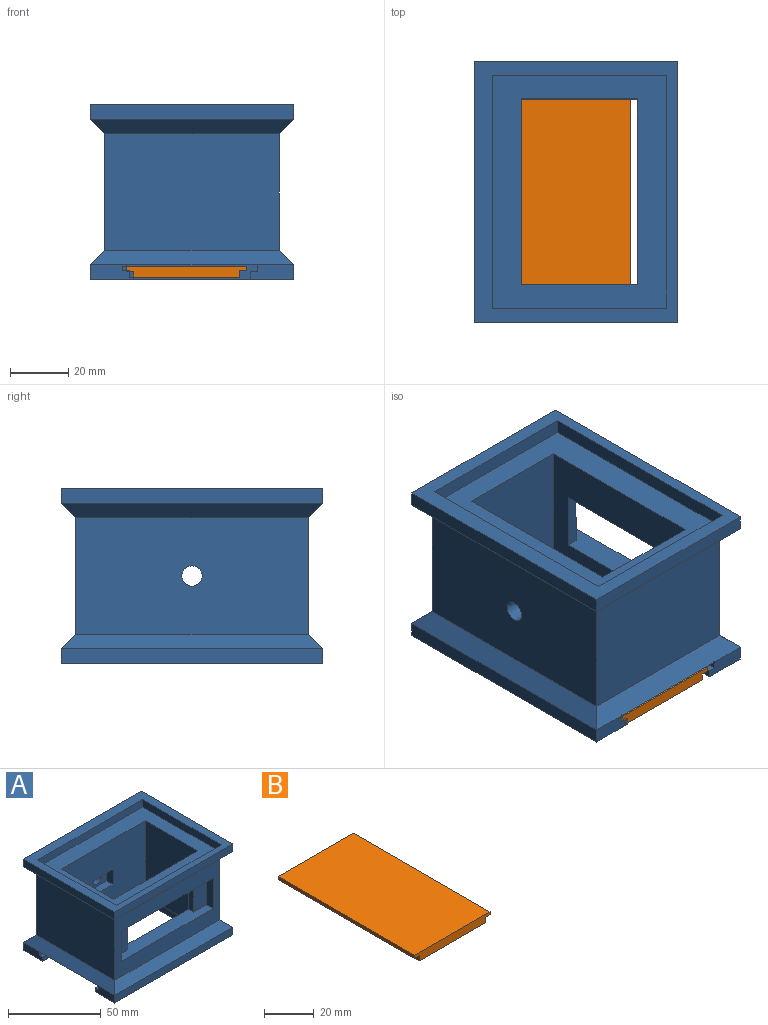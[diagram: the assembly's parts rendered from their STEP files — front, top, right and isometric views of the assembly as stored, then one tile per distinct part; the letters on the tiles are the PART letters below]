
ASSEMBLY  parts=2 mates=1
PART A: 58 faces, bbox 90x70x60 mm
  f0: plane 64x50mm, normal (0,-1,0), area 3050mm2, adj f7,f39,f40,f48,f52,f53,f54,f55
  f1: plane 64x2.5mm, normal (0,1,0), area 160mm2, adj f3,f4,f8,f46
  f2: plane 15x5mm, normal (-1,0,0), area 68.8mm2, adj f8,f13,f21,f43,f46,f47
  f3: plane 2.5x1.11mm, normal (-1,0,0), area 2.8mm2, adj f1,f8,f45,f46
  f4: plane 2.5x1.11mm, normal (1,0,0), area 2.8mm2, adj f1,f8,f43,f46
  f5: plane 20x10mm, normal (0,-1,0), area 200mm2, adj f30,f31,f32,f41
  f6: plane 64x50mm, normal (0,1,0), area 2200mm2, adj f7,f30,f32,f39,f40,f41,f42,f48
  f7: plane 80x60mm, normal (0,0,1), area 2240mm2, adj f0,f6,f35,f36,f37,f38,f39,f40
  f8: plane 90x70mm, normal (0,0,-1), area 3108.9mm2, adj f1,f2,f3,f4,f11,f12,f13,f14
  f9: plane 90x70mm, normal (0,0,1), area 1500mm2, adj f22,f23,f24,f25,f35,f36,f37,f38
  f10: plane 80x40mm, normal (0,-1,0), area 1800mm2, adj f15,f17,f20,f27,f30,f31,f32,f33
  f11: plane 90x5mm, normal (0,1,0), area 450mm2, adj f8,f12,f14,f19
  f12: plane 15x5mm, normal (-1,0,0), area 68.7mm2, adj f8,f11,f21,f44,f49,f50
  f13: plane 90x5mm, normal (0,-1,0), area 450mm2, adj f2,f8,f14,f20
  f14: plane 70x5mm, normal (1,0,0), area 350mm2, adj f8,f11,f13,f18
  f15: plane 60x40mm, normal (1,0,0), area 2400mm2, adj f10,f16,f18,f26
  f16: plane 80x40mm, normal (0,1,0), area 3161.5mm2, adj f15,f17,f19,f28,f57
  f17: plane 60x40mm, normal (-1,0,0), area 2400mm2, adj f10,f16,f21,f29
  f18: plane 70x5mm, normal (0.71,0,0.71), area 459.6mm2, adj f14,f15,f19,f20
  f19: plane 90x5mm, normal (0,0.71,0.71), area 601mm2, adj f11,f16,f18,f21
  f20: plane 90x5mm, normal (0,-0.71,0.71), area 601mm2, adj f10,f13,f18,f21
  f21: plane 70x5mm, normal (-0.71,0,0.71), area 459.6mm2, adj f2,f12,f17,f19,f20,f48
  f22: plane 90x5mm, normal (0,-1,0), area 450mm2, adj f9,f23,f25,f27
  f23: plane 70x5mm, normal (1,0,0), area 350mm2, adj f9,f22,f24,f26
  f24: plane 90x5mm, normal (0,1,0), area 450mm2, adj f9,f23,f25,f28
  f25: plane 70x5mm, normal (-1,0,0), area 350mm2, adj f9,f22,f24,f29
  f26: plane 70x5mm, normal (0.71,0,-0.71), area 459.6mm2, adj f15,f23,f27,f28
  f27: plane 90x5mm, normal (0,-0.71,-0.71), area 601mm2, adj f10,f22,f26,f29
  f28: plane 90x5mm, normal (0,0.71,-0.71), area 601mm2, adj f16,f24,f26,f29
  f29: plane 70x5mm, normal (-0.71,0,-0.71), area 459.6mm2, adj f17,f25,f27,f28
  f30: plane 70x8.89mm, normal (0,0,1), area 544.4mm2, adj f5,f6,f10,f31,f33,f34,f41,f42
  f31: plane 20x5mm, normal (-1,0,0), area 100mm2, adj f5,f10,f30,f32
  f32: plane 70x8.89mm, normal (0,0,-1), area 544.4mm2, adj f5,f6,f10,f31,f33,f34,f41,f42
  f33: plane 20x5mm, normal (1,0,0), area 100mm2, adj f10,f30,f32,f34
  f34: plane 20x10mm, normal (0,-1,0), area 200mm2, adj f30,f32,f33,f42
  f35: plane 80x5mm, normal (0,1,0), area 400mm2, adj f7,f9,f36,f38
  f36: plane 60x5mm, normal (-1,0,0), area 300mm2, adj f7,f9,f35,f37
  f37: plane 80x5mm, normal (0,-1,0), area 400mm2, adj f7,f9,f36,f38
  f38: plane 60x5mm, normal (1,0,0), area 300mm2, adj f7,f9,f35,f37
  f39: plane 50x40mm, normal (-1,0,0), area 2000mm2, adj f0,f6,f7,f48
  f40: plane 50x40mm, normal (1,0,0), area 2000mm2, adj f0,f6,f7,f48
  f41: plane 20x3.89mm, normal (-1,0,0), area 77.8mm2, adj f5,f6,f30,f32
  f42: plane 20x3.89mm, normal (1,0,0), area 77.8mm2, adj f6,f30,f32,f34
  f43: plane 13x2.5mm, normal (0,1,0), area 32.5mm2, adj f2,f4,f8,f46
  f44: plane 78x2.5mm, normal (0,-1,0), area 195mm2, adj f8,f12,f50,f51
  f45: plane 2.5x1mm, normal (0,1,0), area 2.5mm2, adj f3,f8,f46,f51
  f46: plane 78x2.5mm, normal (0,0,1), area 123.9mm2, adj f1,f2,f3,f4,f43,f45,f47,f51
  f47: plane 78x2.5mm, normal (0,1,0), area 195mm2, adj f2,f46,f48,f51
  f48: plane 78x45mm, normal (0,0,-1), area 950mm2, adj f0,f6,f21,f39,f40,f47,f49,f51
  f49: plane 78x2.5mm, normal (0,-1,0), area 195mm2, adj f12,f48,f50,f51
  f50: plane 78x2.5mm, normal (0,0,1), area 195mm2, adj f12,f44,f49,f51
  f51: plane 45x5mm, normal (-1,0,0), area 212.5mm2, adj f8,f44,f45,f46,f47,f48,f49,f50
  f52: plane 10x5mm, normal (-1,0,0), area 50mm2, adj f0,f53,f55,f56
  f53: plane 15x5mm, normal (0,0,-1), area 75mm2, adj f0,f52,f54,f56
  f54: plane 10x5mm, normal (1,0,0), area 50mm2, adj f0,f53,f55,f56
  f55: plane 15x5mm, normal (0,0,1), area 75mm2, adj f0,f52,f54,f56
  f56: plane 15x10mm, normal (0,-1,0), area 111.5mm2, adj f52,f53,f54,f55,f57
  f57: cylinder r=3.5mm len=7mm, axis (0,-1,0), area 134.4mm2, adj f16,f56
PART B: 15 faces, bbox 43x78x4 mm
  f0: plane 78x2.5mm, normal (-1,0,0), area 195mm2, adj f1,f7,f8,f9
  f1: plane 78x38mm, normal (0,0,-1), area 2948mm2, adj f0,f2,f8,f9,f10,f11,f12,f13
  f2: plane 78x2.5mm, normal (1,0,0), area 195mm2, adj f1,f3,f8,f9
  f3: plane 78x2.5mm, normal (0,0,-1), area 195mm2, adj f2,f4,f8,f9
  f4: plane 78x1.5mm, normal (1,0,0), area 117mm2, adj f3,f5,f8,f9
  f5: plane 78x43mm, normal (0,0,1), area 3354mm2, adj f4,f6,f8,f9
  f6: plane 78x1.5mm, normal (-1,0,0), area 117mm2, adj f5,f7,f8,f9
  f7: plane 78x2.5mm, normal (0,0,-1), area 195mm2, adj f0,f6,f8,f9
  f8: plane 43x4mm, normal (0,-1,0), area 159.5mm2, adj f0,f1,f2,f3,f4,f5,f6,f7
  f9: plane 43x4mm, normal (0,1,0), area 159.5mm2, adj f0,f1,f2,f3,f4,f5,f6,f7
  f10: plane 2x1mm, normal (-1,0,0), area 2mm2, adj f1,f11,f13,f14
  f11: plane 8x1mm, normal (0,1,0), area 8mm2, adj f1,f10,f12,f14
  f12: plane 2x1mm, normal (1,0,0), area 2mm2, adj f1,f11,f13,f14
  f13: plane 8x1mm, normal (0,-1,0), area 8mm2, adj f1,f10,f12,f14
  f14: plane 8x2mm, normal (0,0,-1), area 16mm2, adj f10,f11,f12,f13
PLACE A rot(axis=(0,0,1),90deg) t=(34.14,-16.5,79.83)mm
PLACE B t=(25.25,46.29,51.66)mm
MATE pin_slot A.f51 <-> B.f9  axis (0,-1,0) through (-19.14,46.29,82.41)mm
